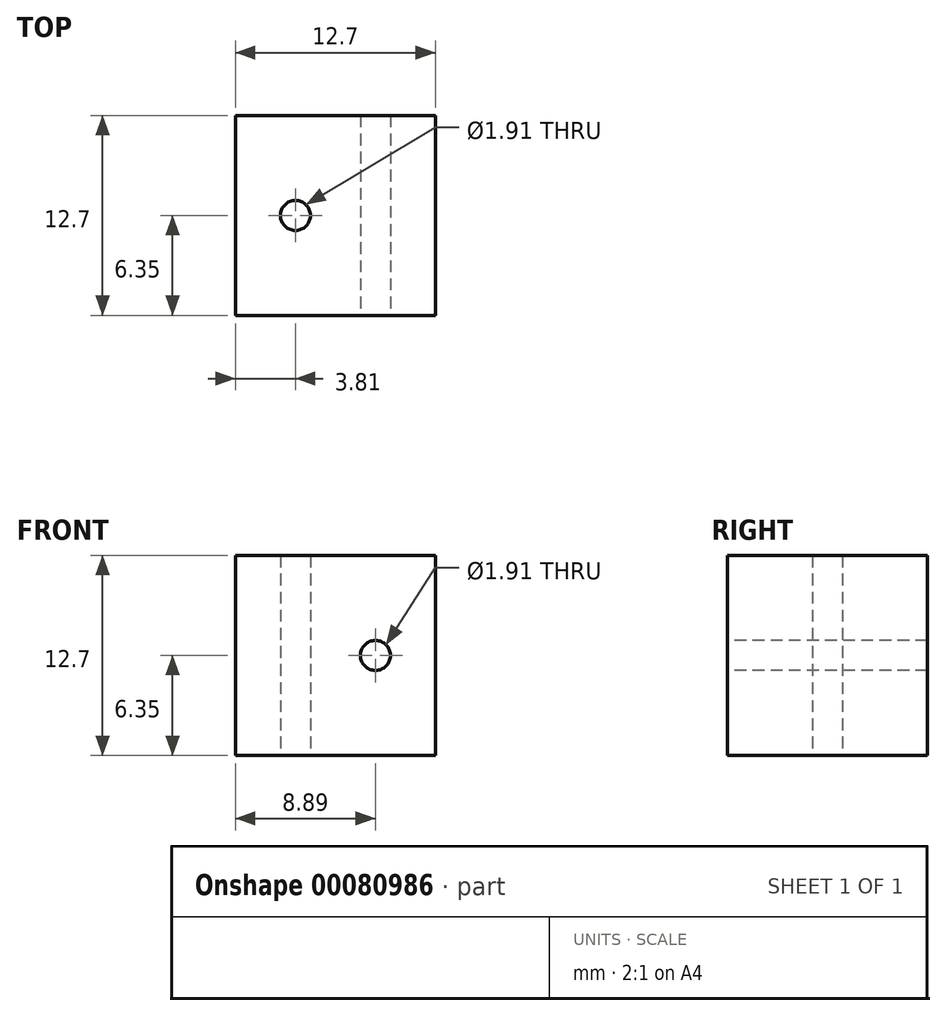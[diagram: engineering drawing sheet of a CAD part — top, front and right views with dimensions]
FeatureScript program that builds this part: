
annotation { "Feature Type Name" : "Feature", "Feature Type Description" : "" }
export const myFeature = defineFeature(function(context is Context, id is Id, definition is map)
    precondition{}
    {
        {
            var Q0;
            Q0=qCreatedBy(makeId("Front.planeOp"),FACE);
            var sketch = newSketch(context, id + "F0", { "sketchPlane" : qUnion([Q0])});
            skLineSegment(sketch, "E0.bottom", {"start": v(0, 0) * mm, "end": v(12.7, 0) * mm});
            skLineSegment(sketch, "E0.top", {"start": v(0, 12.7) * mm, "end": v(12.7, 12.7) * mm});
            skLineSegment(sketch, "E0.left", {"start": v(0, 0) * mm, "end": v(0, 12.7) * mm});
            skLineSegment(sketch, "E0.right", {"start": v(12.7, 0) * mm, "end": v(12.7, 12.7) * mm});
            skSolve(sketch);
        }
        {
            var Q0;
            Q0 = qSketchRegion(id + "F0", true);
            extrude(context, id + "F1", {"entities" : qUnion([Q0]), "depth" : 12.7 * mm});
        }
        {
            var Q0;
            Q0=makeQuery(id+"F1.opExtrude","CAP_FACE",FACE,{"disambiguationData":[OSD([sQuery(id+"F0.wireOp",EDGE,"E0.bottom"),sQuery(id+"F0.wireOp",EDGE,"E0.top"),sQuery(id+"F0.wireOp",EDGE,"E0.left"),sQuery(id+"F0.wireOp",EDGE,"E0.right")])],"isStart":false});
            var sketch = newSketch(context, id + "F2", { "sketchPlane" : qUnion([Q0])});
            skCircle(sketch, "E1", {"center": v(8.9, 6.35) * mm, "radius": 0.95 * mm});
            skSolve(sketch);
        }
        {
            var Q0;
            Q0 = qSketchRegion(id + "F2", true);
            extrude(context, id + "F3", {"entities" : qUnion([Q0]), "operationType" : NewBodyOperationType.REMOVE, "oppositeDirection" : true, "depth" : 25.4 * mm});
        }
        {
            var Q0;
            Q0=makeQuery(id+"F1.opExtrude","SWEPT_FACE",FACE,{"disambiguationData":[OSD([sQuery(id+"F0.wireOp",EDGE,"E0.bottom")])]});
            var sketch = newSketch(context, id + "F4", { "sketchPlane" : qUnion([Q0])});
            skCircle(sketch, "E2", {"center": v(3.81, 6.35) * mm, "radius": 0.95 * mm});
            skSolve(sketch);
        }
        {
            var Q0;
            Q0 = qSketchRegion(id + "F4", true);
            extrude(context, id + "F5", {"entities" : qUnion([Q0]), "operationType" : NewBodyOperationType.REMOVE, "oppositeDirection" : true, "depth" : 25.4 * mm});
        }
    });
